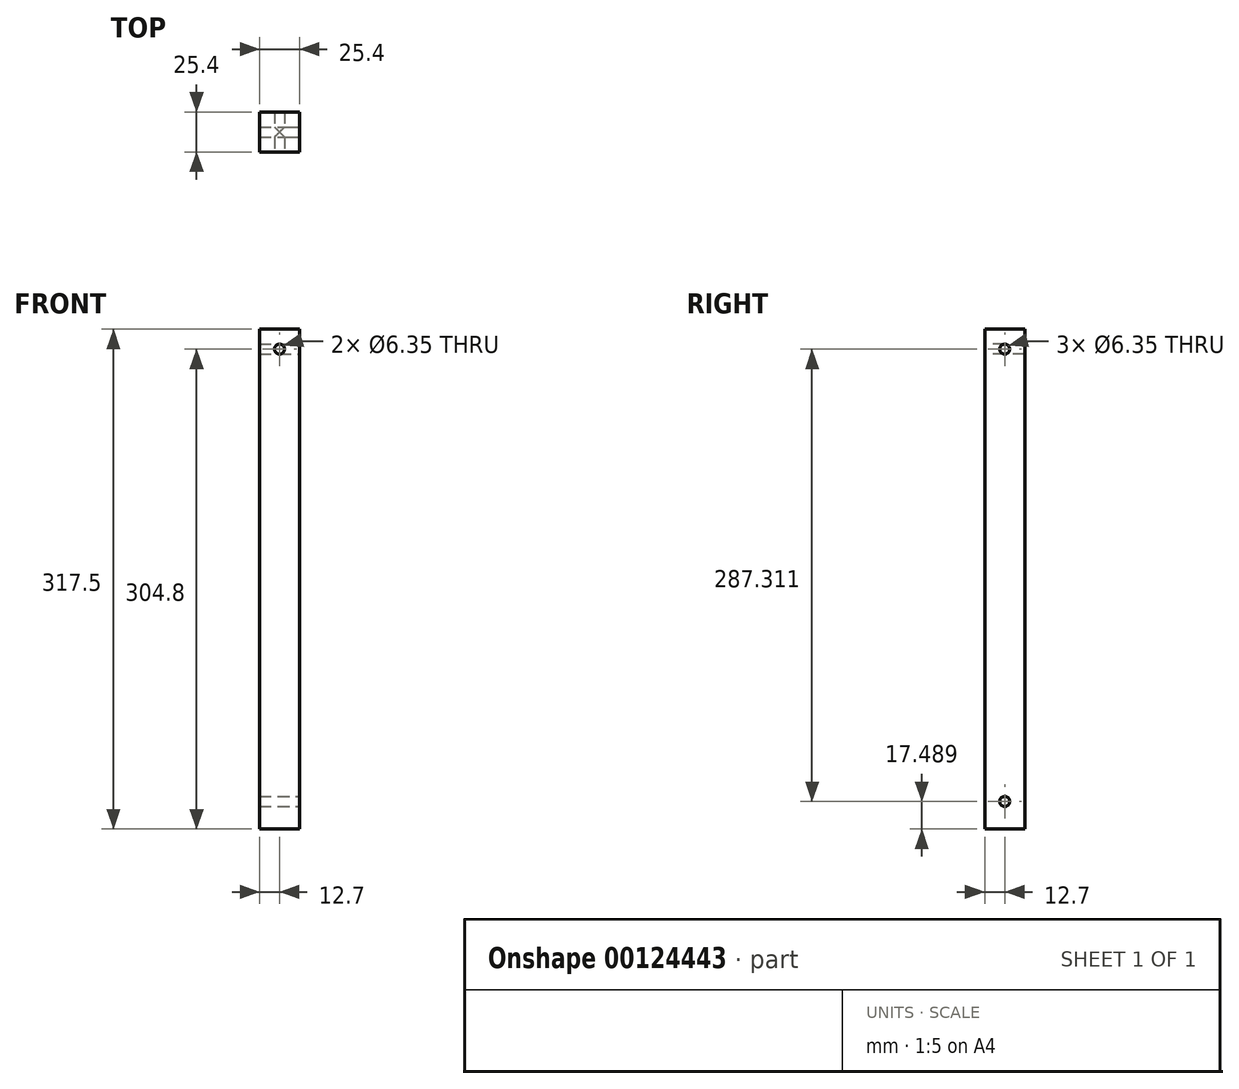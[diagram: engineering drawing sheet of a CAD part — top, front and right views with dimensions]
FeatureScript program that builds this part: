
annotation { "Feature Type Name" : "Feature", "Feature Type Description" : "" }
export const myFeature = defineFeature(function(context is Context, id is Id, definition is map)
    precondition{}
    {
        {
            var Q0;
            Q0=qCreatedBy(makeId("Top.planeOp"),FACE);
            var sketch = newSketch(context, id + "F0", { "sketchPlane" : qUnion([Q0])});
            skLineSegment(sketch, "E0.bottom", {"start": v(12.7, 12.7) * mm, "end": v(-12.7, 12.7) * mm});
            skLineSegment(sketch, "E0.top", {"start": v(12.7, -12.7) * mm, "end": v(-12.7, -12.7) * mm});
            skLineSegment(sketch, "E0.left", {"start": v(12.7, 12.7) * mm, "end": v(12.7, -12.7) * mm});
            skLineSegment(sketch, "E0.right", {"start": v(-12.7, 12.7) * mm, "end": v(-12.7, -12.7) * mm});
            skPoint(sketch, "E0.middle", {"position": v(0, 0) * mm});
            skSolve(sketch);
        }
        {
            var Q0;
            Q0=makeQuery(id+"F0.imprint","IMPRINT",FACE,{"disambiguationData":[TD([[makeQuery(id+"F0.imprint","IMPRINT",EDGE,{"derivedFrom":sQuery(id+"F0.wireOp",EDGE,"E0.bottom")}),1.0]])]});
            extrude(context, id + "F1", {"entities" : qUnion([Q0]), "depth" : 304.8 * mm});
        }
        {
            var Q0;
            Q0=makeQuery(id+"F1.opExtrude","SWEPT_FACE",FACE,{"disambiguationData":[OSD([sQuery(id+"F0.wireOp",EDGE,"E0.top")])]});
            var sketch = newSketch(context, id + "F2", { "sketchPlane" : qUnion([Q0])});
            skLineSegment(sketch, "E1", {"start": v(0, 304.8) * mm, "end": v(0, 0) * mm, "construction": true});
            skLineSegment(sketch, "E2", {"start": v(-12.7, 304.8) * mm, "end": v(-12.7, 292.1) * mm, "construction": true});
            skLineSegment(sketch, "E3", {"start": v(-12.7, 292.1) * mm, "end": v(12.7, 292.1) * mm, "construction": true});
            skCircle(sketch, "E4", {"center": v(0, 292.1) * mm, "radius": 3.18 * mm});
            skSolve(sketch);
        }
        {
            var Q0;
            Q0 = qSketchRegion(id + "F2", true);
            extrude(context, id + "F3", {"entities" : qUnion([Q0]), "operationType" : NewBodyOperationType.REMOVE, "oppositeDirection" : true, "depth" : 50.8 * mm});
        }
        {
            var Q0;
            Q0=makeQuery(id+"F1.opExtrude","SWEPT_FACE",FACE,{"disambiguationData":[OSD([sQuery(id+"F0.wireOp",EDGE,"E0.left")])]});
            var sketch = newSketch(context, id + "F4", { "sketchPlane" : qUnion([Q0])});
            skLineSegment(sketch, "E5", {"start": v(-12.7, 304.8) * mm, "end": v(-12.7, 292.1) * mm, "construction": true});
            skLineSegment(sketch, "E6", {"start": v(-12.7, 292.1) * mm, "end": v(12.7, 292.1) * mm, "construction": true});
            skCircle(sketch, "E7", {"center": v(0, 292.1) * mm, "radius": 3.18 * mm});
            skSolve(sketch);
        }
        {
            var Q0;
            Q0=makeQuery(id+"F4.imprint","IMPRINT",FACE,{"disambiguationData":[TD([[makeQuery(id+"F4.imprint","IMPRINT",EDGE,{"derivedFrom":sQuery(id+"F4.wireOp",EDGE,"E7")}),1.0]])]});
            extrude(context, id + "F5", {"entities" : qUnion([Q0]), "operationType" : NewBodyOperationType.REMOVE, "oppositeDirection" : true, "depth" : 25.4 * mm});
        }
        {
            var Q0;
            Q0=makeQuery(id+"F1.opExtrude","SWEPT_FACE",FACE,{"disambiguationData":[OSD([sQuery(id+"F0.wireOp",EDGE,"E0.left")])]});
            var sketch = newSketch(context, id + "F6", { "sketchPlane" : qUnion([Q0])});
            skLineSegment(sketch, "E8", {"start": v(0, 0) * mm, "end": v(0, 4.79) * mm, "construction": true});
            skCircle(sketch, "E9", {"center": v(0, 4.79) * mm, "radius": 3.18 * mm});
            skSolve(sketch);
        }
        {
            var Q0;
            Q0=makeQuery(id+"F6.imprint","IMPRINT",FACE,{"disambiguationData":[TD([[makeQuery(id+"F6.imprint","IMPRINT",EDGE,{"derivedFrom":sQuery(id+"F6.wireOp",EDGE,"E9")}),1.0]])]});
            var Q1;
            Q1=sQuery(id+"F6.wireOp",EDGE,"E9");
            extrude(context, id + "F7", {"entities" : qUnion([Q0]), "operationType" : NewBodyOperationType.REMOVE, "surfaceEntities" : qUnion([Q1]), "oppositeDirection" : true, "depth" : 25.4 * mm});
        }
        {
            var Q0;
            Q0=makeQuery(id+"F1.opExtrude","CAP_FACE",FACE,{"disambiguationData":[OSD([sQuery(id+"F0.wireOp",EDGE,"E0.bottom"),sQuery(id+"F0.wireOp",EDGE,"E0.top"),sQuery(id+"F0.wireOp",EDGE,"E0.left"),sQuery(id+"F0.wireOp",EDGE,"E0.right")])],"isStart":true});
            extrude(context, id + "F8", {"entities" : qUnion([Q0]), "operationType" : NewBodyOperationType.ADD, "depth" : 12.7 * mm});
        }
    });
